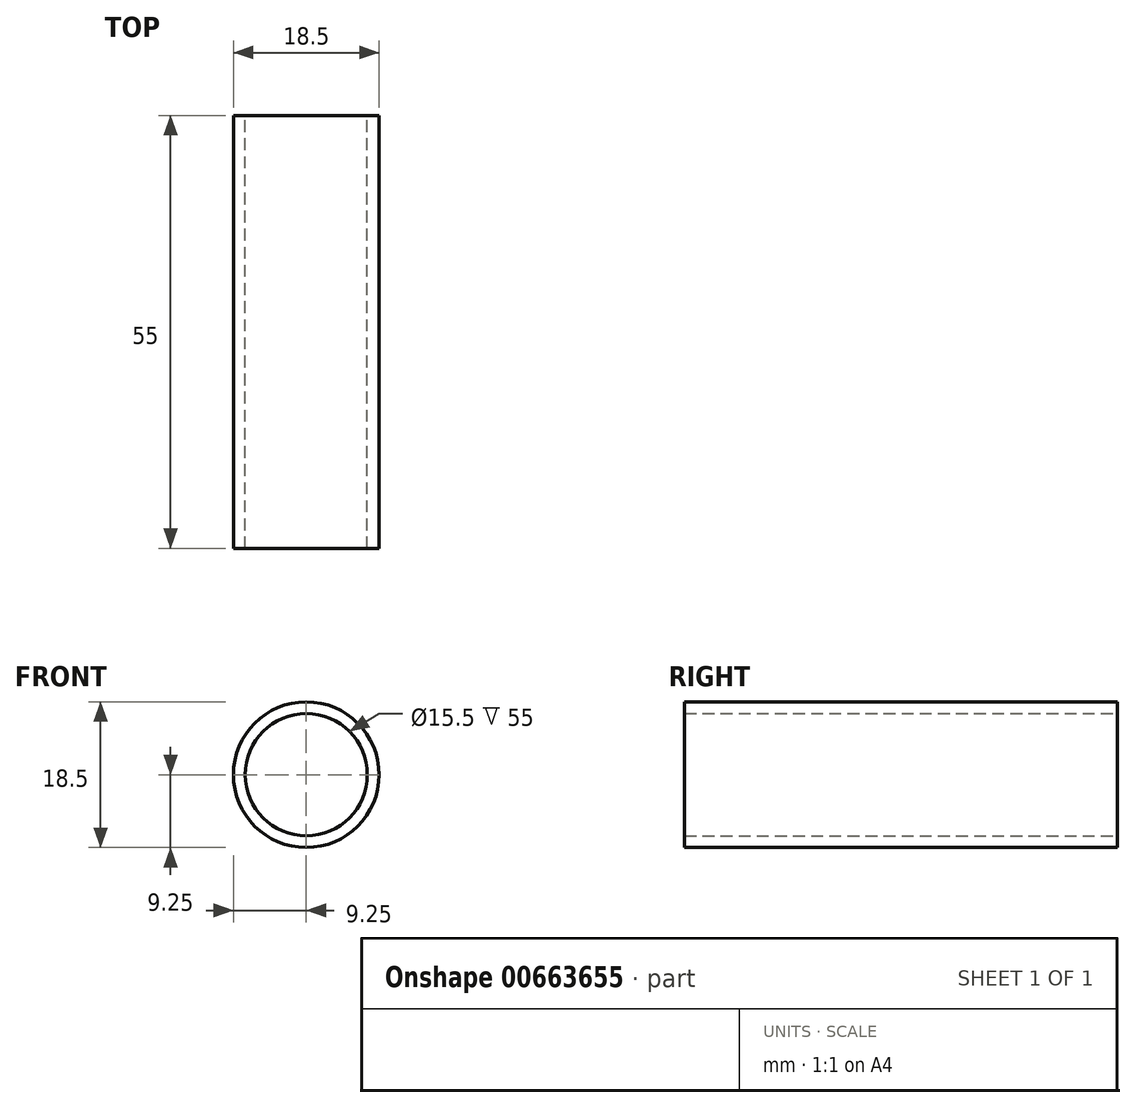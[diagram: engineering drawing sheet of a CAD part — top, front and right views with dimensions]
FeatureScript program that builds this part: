
annotation { "Feature Type Name" : "Feature", "Feature Type Description" : "" }
export const myFeature = defineFeature(function(context is Context, id is Id, definition is map)
    precondition{}
    {
        {
            var Q0;
            Q0=qCreatedBy(makeId("Front.planeOp"),FACE);
            var sketch = newSketch(context, id + "F0", { "sketchPlane" : qUnion([Q0])});
            skCircle(sketch, "E0", {"center": v(0, 0) * mm, "radius": 9.25 * mm});
            skCircle(sketch, "E1.0", {"center": v(0, 0) * mm, "radius": 7.75 * mm});
            skSolve(sketch);
        }
        {
            var Q0;
            Q0=qSketchRegion(id+"F0",true);
            extrude(context, id + "F1", {"entities" : qUnion([Q0]), "depth" : 55 * mm, "offsetDistance" : 25 * mm});
        }
    });
